# Revit family: ROTHOB_Rothoblaas_Membrane_ClimaControlNet160
name_source: partatom
category: Structural Connections
units: mm (PartAtom-declared; Revit-internal decimal feet)

## family parameters
Cut with Voids When Loaded = No
Enable cutting in views = Yes
Host = Face
Material for Model Behavior = Other
OmniClass Number = 23.13.25.25
OmniClass Title = Air Barriers
Shared = No

## types (1)
- WIDTHxHEIGHTmm
    BIMObjectName = ROTHOB_Rothoblaas_Membrane_ClimaControlNet160
    CECode = EN 13984
    CodePerformance = CE - Construction products
    Color = Grey
    Default Elevation = 1.22 m
    Description = Membrane with variable vapour diffusion and reinforcement grid
    DurationUnit = Years
    EPDCode = 2021M10140
    Esporta tipo in formato IFC con nome = IfcBuildingElementProxyType
    Features = Flexible sheets for waterproofing - Plastic and rubber vapour control layers
    Finish = Polypropylene
    IfcExportAs = IfcBuildingElementProxyType
    IfcExportType = USERDEFINED
    ManufacturerName = ROTHO BLAAS SRL
    ManufacturerURL = www.rothoblaas.com
    MassUnitArea = 160 g/m2
    Material = Polyamide and polypropylene
    ModelDisclaimer = The latest version of the data sheets can be found on our website
    Name = Membrane
    ObjectMaterial = ROTHOB_Rothoblaas_Polyamide_Polypropylene
    OmniClassCode = 23.13.25.25
    OmniClassTitle = Air Barriers
    OmniClassVersion = 2012-05-16
    ProductInformation = https://www.rothoblaas.com
    ReactionFire = class E
    Shape = Bidimensional
    Tipo IFC predefinito = USERDEFINED
    UVStability = 336h (3 months)
    VariableWaterVapourTransmition_Sd = 0,5/5 m
    Version = 2
